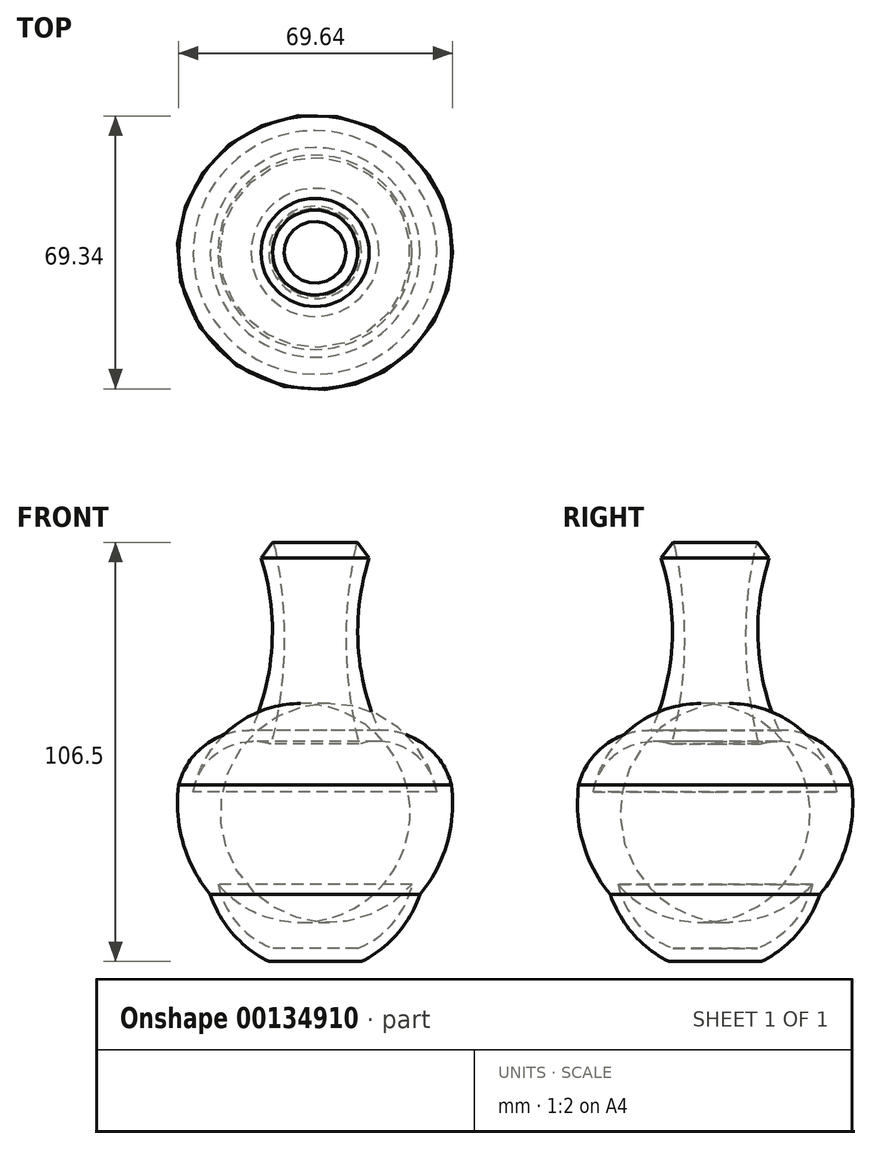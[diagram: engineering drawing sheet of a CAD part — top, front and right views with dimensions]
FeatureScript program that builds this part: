
annotation { "Feature Type Name" : "Feature", "Feature Type Description" : "" }
export const myFeature = defineFeature(function(context is Context, id is Id, definition is map)
    precondition{}
    {
        {
            var Q0;
            Q0=qCreatedBy(makeId("Front.planeOp"),FACE);
            var sketch = newSketch(context, id + "F0", { "sketchPlane" : qUnion([Q0])});
            skLineSegment(sketch, "E0", {"start": v(0, -50.43) * mm, "end": v(11.75, -50.43) * mm});
            skArc(sketch, "E1", {"start": v(11.75, -50.43) * mm, "mid": v(20.86, -43.37) * mm, "end": v(26.64, -33.4) * mm});
            skArc(sketch, "E2", {"start": v(26.64, -33.4) * mm, "mid": v(33.55, -20.33) * mm, "end": v(34.67, -5.58) * mm});
            skArc(sketch, "E3", {"start": v(34.67, -5.58) * mm, "mid": v(27.91, 4.61) * mm, "end": v(16.26, 8.32) * mm});
            skArc(sketch, "E4", {"start": v(16.26, 58.66) * mm, "mid": v(10.84, 33.5) * mm, "end": v(16.26, 8.32) * mm});
            skLineSegment(sketch, "E5", {"start": v(16.26, 58.66) * mm, "end": v(11.16, 58.66) * mm});
            skArc(sketch, "E6", {"start": v(11.16, 58.66) * mm, "mid": v(7.85, 31.73) * mm, "end": v(11.16, 4.8) * mm});
            skArc(sketch, "E7", {"start": v(30.95, -7.34) * mm, "mid": v(23.84, 3.27) * mm, "end": v(11.16, 4.8) * mm});
            skArc(sketch, "E8", {"start": v(24.68, -30.85) * mm, "mid": v(30.52, -19.82) * mm, "end": v(30.95, -7.34) * mm});
            skArc(sketch, "E9", {"start": v(10.77, -47.1) * mm, "mid": v(19.75, -40.7) * mm, "end": v(24.68, -30.85) * mm});
            skLineSegment(sketch, "E10", {"start": v(10.77, -47.1) * mm, "end": v(0, -47.1) * mm});
            skLineSegment(sketch, "E11", {"start": v(0, -47.1) * mm, "end": v(0, -50.43) * mm});
            skSolve(sketch);
        }
        {
            var Q0;
            Q0=makeQuery(id+"F0.imprint","IMPRINT",FACE,{"disambiguationData":[TD([[makeQuery(id+"F0.imprint","IMPRINT",EDGE,{"derivedFrom":sQuery(id+"F0.wireOp",EDGE,"E0")}),1.0]])]});
            var Q1;
            Q1=sQuery(id+"F0.wireOp",EDGE,"E11");
            revolve(context, id + "F1", {"entities" : qUnion([Q0]), "axis" : qUnion([Q1]), "revolveType" : RevolveType.FULL});
        }
        {
            var Q0;
            Q0=makeQuery(id+"F1.opRevolve","SWEPT_EDGE",EDGE,{"disambiguationData":[OSD([sQuery(id+"F0.wireOp",EDGE,"E5"),sQuery(id+"F0.wireOp",EDGE,"E6")])]});
            fillet(context, id + "F2", {"entities" : qUnion([Q0]), "radius" : 5.08 * mm, "tangentPropagation" : true, "allowEdgeOverflow" : false});
        }
        {
            var Q0;
            Q0=makeQuery(id+"F1.opRevolve","SWEPT_EDGE",EDGE,{"disambiguationData":[OSD([sQuery(id+"F0.wireOp",EDGE,"E4"),sQuery(id+"F0.wireOp",EDGE,"E5")])]});
            chamfer(context, id + "F3", {"entities" : qUnion([Q0]), "width" : 5.08 * mm, "tangentPropagation" : true});
        }
    });
